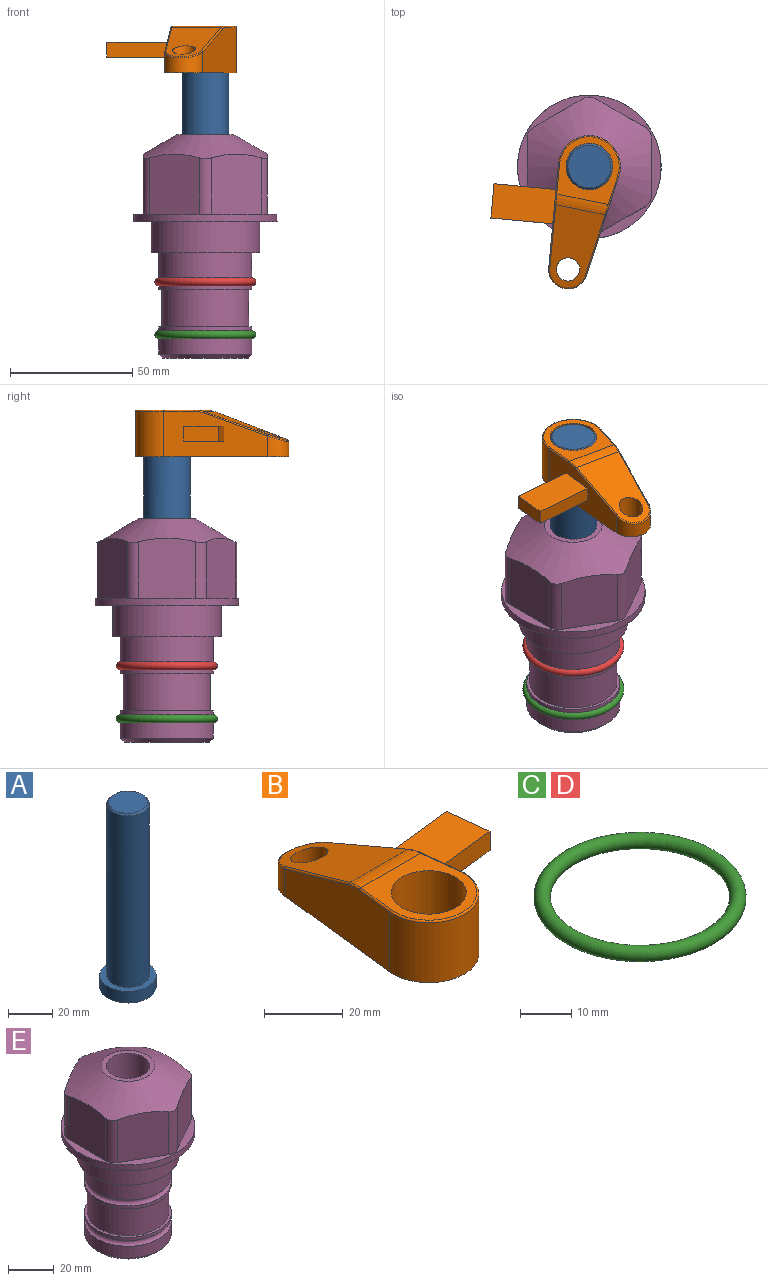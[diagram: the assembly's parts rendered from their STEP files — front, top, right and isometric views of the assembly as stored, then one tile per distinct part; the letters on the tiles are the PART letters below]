
ASSEMBLY  parts=5 mates=3
PART A: 6 faces, bbox 25.4x25.4x101.6 mm
  f0: plane 17.46x17.46mm, normal (0,0,1), area 239.5mm2, adj f5
  f1: plane 25.4x25.4mm, normal (0,0,-1), area 506.7mm2, adj f2
  f2: cylinder r=12.7mm len=25.4mm, axis (0,0,1), area 506.7mm2, adj f1,f3
  f3: plane 25.4x25.4mm, normal (0,0,1), area 221.7mm2, adj f2,f4
  f4: cylinder r=9.53mm len=94.46mm, axis (0,0,1), area 5653mm2, adj f3,f5
  f5: cone r=8.73mm half-angle=45deg, axis (0,0,-1), area 64.4mm2, adj f0,f4
PART B: 49 faces, bbox 50.4x64.5x19.1 mm
  f0: plane 2.3x0.95mm, normal (0,0,-1), area 1mm2, adj f25,f30,f34
  f1: plane 63.5x25.4mm, normal (0,0,-1), area 561.7mm2, adj f2,f3,f4,f5,f6,f7,f19,f20
  f2: cylinder r=12.7mm len=25.4mm, axis (0,0,-1), area 792.2mm2, adj f1,f3,f5,f13
  f3: plane 42.33x18.54mm, normal (0.99,0.11,0), area 563.1mm2, adj f1,f2,f4,f11,f12,f14,f44,f45
  f4: cylinder r=7.94mm len=15.78mm, axis (0,0,-1), area 158.6mm2, adj f1,f3,f5,f16
  f5: plane 42.33x18.54mm, normal (-0.99,0.11,0), area 647mm2, adj f1,f2,f4,f15,f17,f18
  f6: cylinder r=9.53mm len=19.05mm, axis (0,0,-1), area 1140.1mm2, adj f1,f8
  f7: cylinder r=4.76mm len=10.98mm, axis (0,0,-1), area 276.1mm2, adj f1,f9
  f8: plane 25.83x24.38mm, normal (0,0,1), area 262.2mm2, adj f6,f10,f11,f13,f15
  f9: plane 32.49x20.55mm, normal (0,0.34,0.94), area 489.9mm2, adj f7,f10,f14,f16,f18
  f10: cylinder r=12.7mm len=21.49mm, axis (-1,0,0), area 93.2mm2, adj f8,f9,f12,f17
  f11: cylinder r=0.51mm len=12.34mm, axis (0.11,-0.99,0), area 9.9mm2, adj f3,f8,f12,f13
  f12: bspline ~7.62x1.64mm, area 3.5mm2, adj f3,f10,f11,f14
  f13: torus R=12.19mm, axis (0,0,1), area 33.6mm2, adj f2,f8,f11,f15
  f14: cylinder r=0.51mm len=26.01mm, axis (0.1,-0.93,0.34), area 21.6mm2, adj f3,f9,f12,f16
  f15: cylinder r=0.51mm len=12.34mm, axis (0.11,0.99,0), area 9.9mm2, adj f5,f8,f13,f17
  f16: bspline ~15.78x7.05mm, area 15.7mm2, adj f4,f9,f14,f18
  f17: bspline ~7.62x1.64mm, area 3.5mm2, adj f5,f10,f15,f18
  f18: cylinder r=0.51mm len=26.01mm, axis (0.1,0.93,-0.34), area 21.6mm2, adj f5,f9,f16,f17
  f19: plane 21.6x14.29mm, normal (-0.99,-0.11,0), area 242.6mm2, adj f1,f26,f28,f34,f36,f38
  f20: plane 21.6x14.29mm, normal (0.99,-0.11,0), area 242.6mm2, adj f1,f27,f29,f37,f39,f41
  f21: cylinder r=12.7mm len=14.29mm, axis (0,0,-1), area 173.2mm2, adj f1,f26,f27,f30,f31,f33
  f22: cylinder r=7.94mm len=7.63mm, axis (0,0,-1), area 53.8mm2, adj f1,f28,f29,f42
  f23: plane 2.3x0.95mm, normal (0,0,-1), area 1mm2, adj f25,f33,f37
  f24: plane 17.94x12.32mm, normal (0,-0.34,-0.94), area 191.2mm2, adj f25,f38,f41,f42
  f25: cylinder r=9.53mm len=12.93mm, axis (-1,0,0), area 37.5mm2, adj f0,f23,f24,f31,f36,f39
  f26: cylinder r=1.59mm len=14.29mm, axis (0,0,-1), area 49mm2, adj f1,f19,f21,f32
  f27: cylinder r=1.59mm len=14.29mm, axis (0,0,-1), area 49mm2, adj f1,f20,f21,f35
  f28: cylinder r=1.59mm len=7.28mm, axis (0,0,-1), area 22.1mm2, adj f1,f19,f22,f40
  f29: cylinder r=1.59mm len=7.28mm, axis (0,0,-1), area 22.1mm2, adj f1,f20,f22,f43
  f30: torus R=14.29mm, axis (0,0,1), area 5.8mm2, adj f0,f21,f31,f32
  f31: bspline ~11.06x2.73mm, area 20.8mm2, adj f21,f25,f30,f33
  f32: sphere r=1.59mm, area 5.4mm2, adj f26,f30,f34
  f33: torus R=14.29mm, axis (0,0,1), area 5.8mm2, adj f21,f23,f31,f35
  f34: cylinder r=1.59mm len=1.68mm, axis (-0.11,0.99,0), area 2.4mm2, adj f0,f19,f32,f36
  f35: sphere r=1.59mm, area 5.4mm2, adj f27,f33,f37
  f36: bspline ~5.82x2.33mm, area 7.7mm2, adj f19,f25,f34,f38
  f37: cylinder r=1.59mm len=1.68mm, axis (0.11,0.99,0), area 2.4mm2, adj f20,f23,f35,f39
  f38: cylinder r=1.59mm len=18.33mm, axis (0.1,-0.93,0.34), area 46.7mm2, adj f19,f24,f36,f40
  f39: bspline ~5.82x2.33mm, area 7.7mm2, adj f20,f25,f37,f41
  f40: sphere r=1.59mm, area 3.6mm2, adj f28,f38,f42
  f41: cylinder r=1.59mm len=18.33mm, axis (0.1,0.93,-0.34), area 46.7mm2, adj f20,f24,f39,f43
  f42: bspline ~8.31x1.84mm, area 15.3mm2, adj f22,f24,f40,f43
  f43: sphere r=1.59mm, area 3.6mm2, adj f29,f41,f42
  f44: plane 26.81x16.8mm, normal (0,0,1), area 357.2mm2, adj f3,f45,f47,f48
  f45: plane 25.24x5.97mm, normal (0.11,-0.99,0), area 151.6mm2, adj f3,f44,f46,f48
  f46: plane 26.81x16.8mm, normal (0,0,-1), area 357.2mm2, adj f3,f45,f47,f48
  f47: plane 25.24x5.97mm, normal (-0.11,0.99,0), area 151.6mm2, adj f3,f44,f46,f48
  f48: plane 13.98x5.97mm, normal (0.99,0.11,0), area 83.9mm2, adj f44,f45,f46,f47
PART C: 1 faces, bbox 44.7x44.7x3.2 mm
  f0: torus R=19.05mm, axis (0,0,1), area 1193.9mm2
PART D: same geometry as C
PART E: 36 faces, bbox 58.7x58.7x91.2 mm
  f0: cylinder r=17.78mm len=35.56mm, axis (0,0,1), area 1670.8mm2, adj f23,f24,f31
  f1: cylinder r=19.05mm len=38.1mm, axis (0,0,1), area 1191.9mm2, adj f26,f27,f30
  f2: plane 58.66x58.66mm, normal (0,0,-1), area 1150.6mm2, adj f3,f28
  f3: cylinder r=29.33mm len=58.66mm, axis (0,0,-1), area 585.1mm2, adj f2,f4
  f4: plane 58.66x58.66mm, normal (0,0,1), area 475.9mm2, adj f3,f5,f6,f7,f8,f9,f10,f11
  f5: plane 24.5x20.32mm, normal (-0.5,0.87,0), area 562.8mm2, adj f4,f15,f16,f17
  f6: plane 24.5x20.32mm, normal (0.5,0.87,0), area 562.8mm2, adj f4,f14,f15,f17
  f7: plane 24.5x23.48mm, normal (1,0,0), area 562.8mm2, adj f4,f13,f14,f17
  f8: plane 24.5x20.32mm, normal (0.5,-0.87,0), area 562.8mm2, adj f4,f12,f13,f17
  f9: plane 24.5x20.32mm, normal (-0.5,-0.87,0), area 562.8mm2, adj f4,f11,f12,f17
  f10: plane 24.5x23.48mm, normal (-1,0,0), area 562.8mm2, adj f4,f11,f16,f17
  f11: cylinder r=5.08mm len=23.01mm, axis (0,0,-1), area 121.2mm2, adj f4,f9,f10,f17
  f12: cylinder r=5.08mm len=23.01mm, axis (0,0,-1), area 121.2mm2, adj f4,f8,f9,f17
  f13: cylinder r=5.08mm len=23.01mm, axis (0,0,-1), area 121.2mm2, adj f4,f7,f8,f17
  f14: cylinder r=5.08mm len=23.01mm, axis (0,0,-1), area 121.2mm2, adj f4,f6,f7,f17
  f15: cylinder r=5.08mm len=23.01mm, axis (0,0,-1), area 121.2mm2, adj f4,f5,f6,f17
  f16: cylinder r=5.08mm len=23.01mm, axis (0,0,-1), area 121.2mm2, adj f4,f5,f10,f17
  f17: cone r=11.73mm half-angle=60deg, axis (0,0,-1), area 2071.8mm2, adj f5,f6,f7,f8,f9,f10,f11,f12
  f18: plane 23.46x23.46mm, normal (0,0,1), area 147.4mm2, adj f17,f35
  f19: plane 34.93x34.93mm, normal (0,0,-1), area 958mm2, adj f29
  f20: cylinder r=19.05mm len=38.1mm, axis (0,0,1), area 760.1mm2, adj f21,f29
  f21: torus R=19.05mm, axis (0,0,1), area 565.3mm2, adj f20,f22
  f22: cylinder r=19.05mm len=38.1mm, axis (0,0,1), area 190mm2, adj f21,f23
  f23: plane 38.1x38.1mm, normal (0,0,1), area 146.9mm2, adj f0,f22
  f24: plane 38.1x38.1mm, normal (0,0,-1), area 146.9mm2, adj f0,f25
  f25: cylinder r=19.05mm len=38.1mm, axis (0,0,1), area 190mm2, adj f24,f26
  f26: torus R=19.05mm, axis (0,0,1), area 565.3mm2, adj f1,f25
  f27: plane 44.45x44.45mm, normal (0,0,-1), area 411.7mm2, adj f1,f28
  f28: cylinder r=22.23mm len=44.45mm, axis (0,0,1), area 1773.5mm2, adj f2,f27
  f29: cone r=19.05mm half-angle=45deg, axis (0,0,1), area 257.5mm2, adj f19,f20
  f30: cylinder r=3.17mm len=6.75mm, axis (-1,0,0), area 128mm2, adj f1,f33
  f31: cylinder r=3.17mm len=6.35mm, axis (-1,0,0), area 102.5mm2, adj f0,f33
  f32: plane 25.4x25.4mm, normal (0,0,1), area 506.7mm2, adj f33
  f33: cylinder r=12.7mm len=66.42mm, axis (0,0,-1), area 5236.2mm2, adj f30,f31,f32,f34
  f34: cone r=9.53mm half-angle=30deg, axis (0,0,-1), area 443.4mm2, adj f33,f35
  f35: cylinder r=9.53mm len=19.05mm, axis (0,0,-1), area 849mm2, adj f18,f34
PLACE A rot(axis=(0,0,-1),101.7deg) t=(0,0,6.38)mm
PLACE B rot(axis=(0,0,1),168.3deg) t=(0,0,60.99)mm
PLACE C t=(0,0,-21.59)mm
PLACE D at identity
PLACE E at identity fixed
MATE fastened C.f0 <-> E.f0  axis (0,0,1) through (0,0,-46.1)mm
MATE cylindrical A.f2 <-> E.f0  axis (0,0,1) through (0,0,32.01)mm
MATE fastened B.f2 <-> A.f2  axis (0,0,1) through (0,0,80.04)mm
